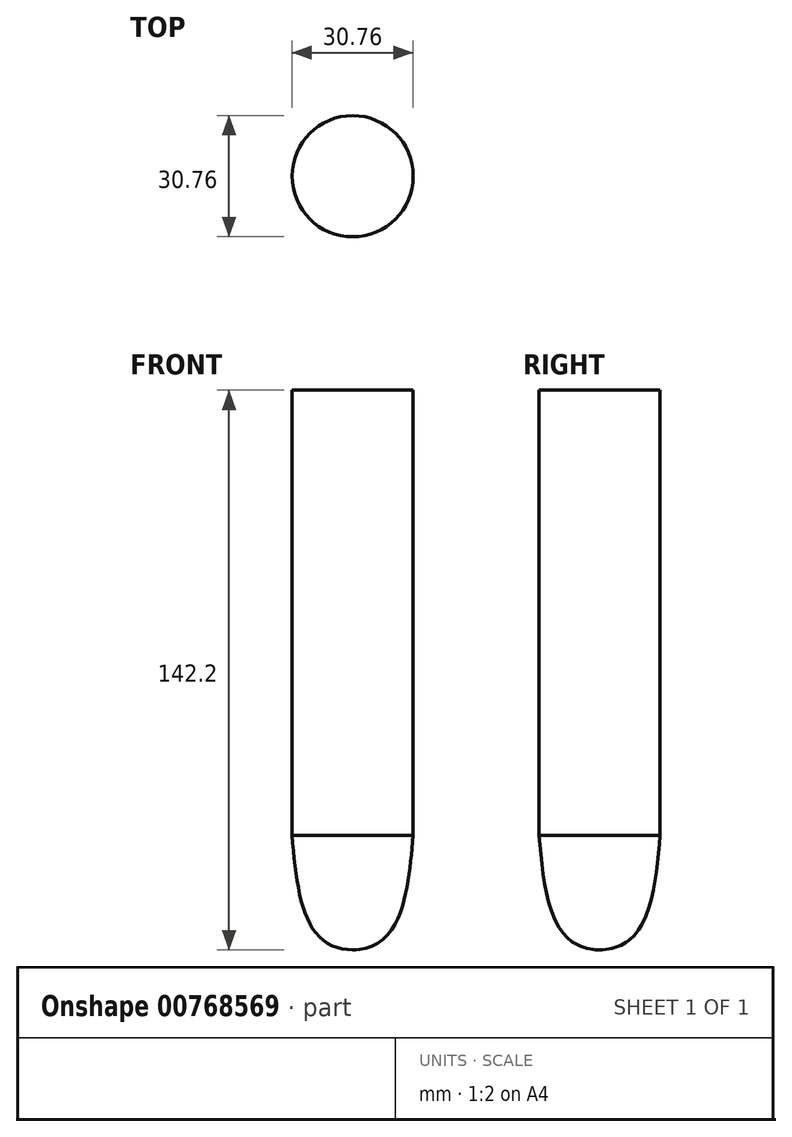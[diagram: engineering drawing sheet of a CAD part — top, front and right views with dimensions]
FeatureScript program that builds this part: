
annotation { "Feature Type Name" : "Feature", "Feature Type Description" : "" }
export const myFeature = defineFeature(function(context is Context, id is Id, definition is map)
    precondition{}
    {
        {
            var Q0;
            Q0=qCreatedBy(makeId("Front.planeOp"),FACE);
            var sketch = newSketch(context, id + "F0", { "sketchPlane" : qUnion([Q0])});
            skLineSegment(sketch, "E0", {"start": v(0, 0) * mm, "end": v(30.76, 0) * mm});
            skLineSegment(sketch, "E1", {"start": v(30.76, 0) * mm, "end": v(30.76, 113.1) * mm});
            skLineSegment(sketch, "E2", {"start": v(0, 90.97) * mm, "end": v(0, 0) * mm});
            skLineSegment(sketch, "E3", {"start": v(15.38, 90.97) * mm, "end": v(15.38, -29.1) * mm});
            skLineSegment(sketch, "E4", {"start": v(15.38, 0) * mm, "end": v(30.76, 0) * mm});
            skLineSegment(sketch, "E5", {"start": v(15.38, 0) * mm, "end": v(0, 0) * mm});
            skFitSpline(sketch, "E6", {"points": [v(0, 0) * mm, v(7.7, -26.49) * mm, v(23.07, -26.49) * mm, v(30.76, 0) * mm], "startDerivative": vector(8.22, -89.9) * mm, "endDerivative": vector(8.22, 89.9) * mm});
            skPoint(sketch, "E7.start.orphan", {"position": v(23.07, 0) * mm});
            skPoint(sketch, "E8.end.orphan", {"position": v(15.38, -26.49) * mm});
            skPoint(sketch, "E9.start.orphan", {"position": v(7.7, 0) * mm});
            skLineSegment(sketch, "E10", {"start": v(30.76, 113.1) * mm, "end": v(0, 113.1) * mm});
            skLineSegment(sketch, "E11", {"start": v(0, 113.1) * mm, "end": v(0, 90.97) * mm});
            skLineSegment(sketch, "E12", {"start": v(15.38, 90.97) * mm, "end": v(15.38, 113.1) * mm});
            skPoint(sketch, "E13.orphan", {"position": v(30.76, 90.97) * mm});
            skSolve(sketch);
        }
        {
            var Q0;
            {var subQ6=sQuery(id+"F0.wireOp",EDGE,"E2");Q0=makeQuery(id+"F0.imprint","IMPRINT",FACE,{"disambiguationData":[TD([[makeQuery(id+"F0.imprint","IMPRINT",EDGE,{"derivedFrom":subQ6}),1.0]])]});}
            var Q1;
            {var subQ0=sQuery(id+"F0.wireOp",EDGE,"E6");var subQ3=sQuery(id+"F0.wireOp",EDGE,"E3");var subQ5=makeQuery(id+"F0.imprint","INTERSECT",VERTEX,{"derivedFrom":[subQ3,subQ0]});Q1=makeQuery(id+"F0.imprint","IMPRINT",FACE,{"disambiguationData":[TD([[makeQuery(id+"F0.imprint","IMPRINT",EDGE,{"disambiguationData":[TD([[subQ5,1.0]])],"derivedFrom":subQ3}),-1.0]])]});}
            var Q2;
            Q2=sQuery(id+"F0.wireOp",EDGE,"E3");
            revolve(context, id + "F1", {"surfaceOperationType" : NewSurfaceOperationType.NEW, "entities" : qUnion([Q0, Q1]), "axis" : qUnion([Q2]), "revolveType" : RevolveType.FULL});
        }
    });
